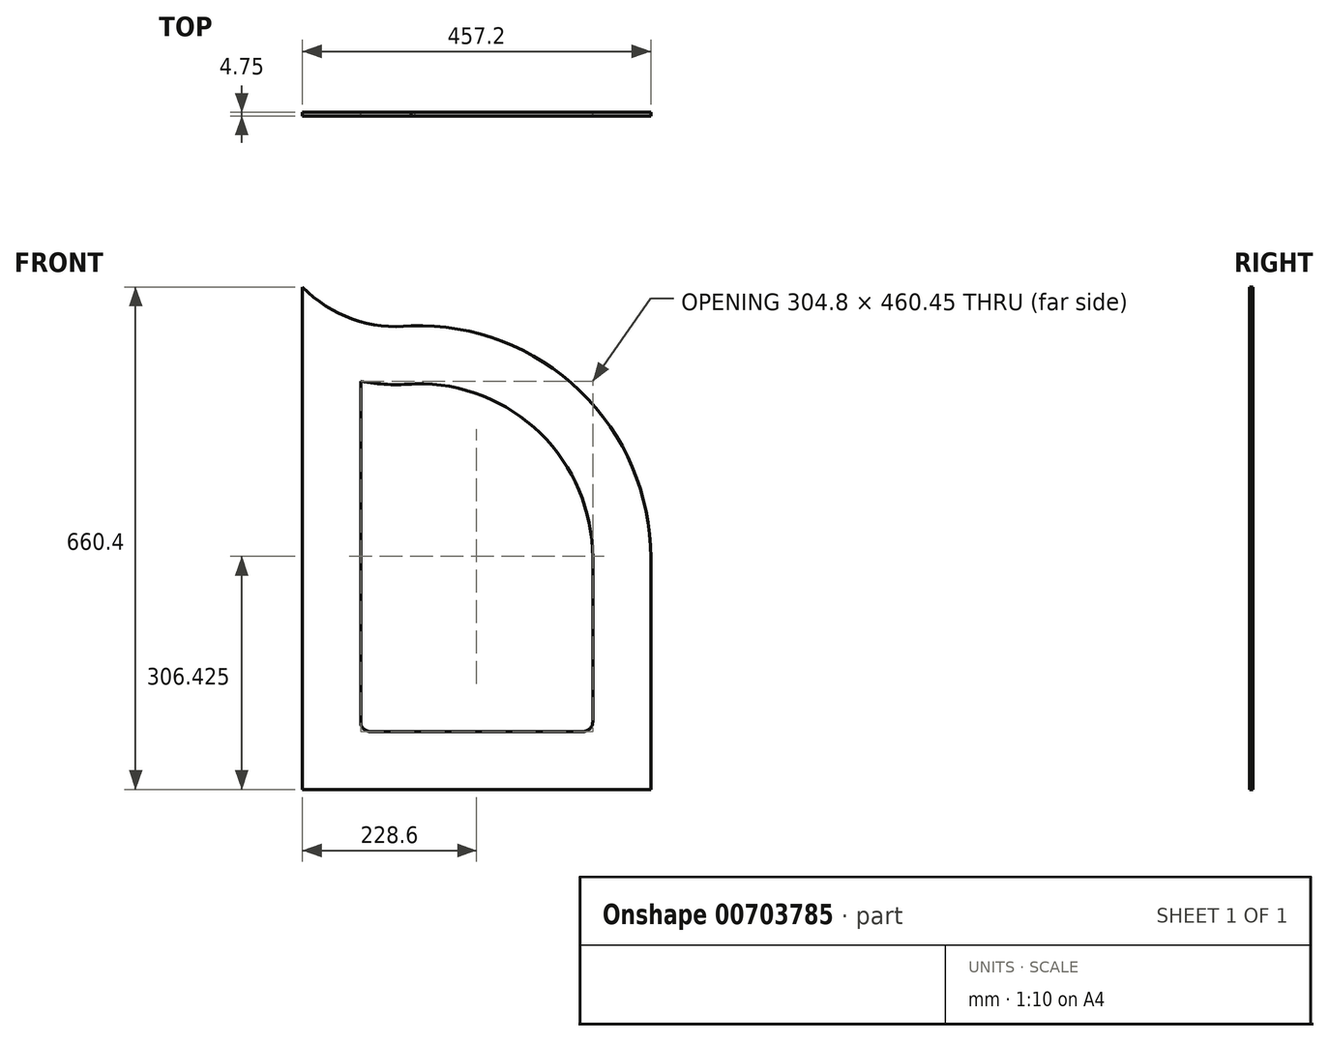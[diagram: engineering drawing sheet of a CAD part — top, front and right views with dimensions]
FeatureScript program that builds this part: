
annotation { "Feature Type Name" : "Feature", "Feature Type Description" : "" }
export const myFeature = defineFeature(function(context is Context, id is Id, definition is map)
    precondition{}
    {
        {
            var Q0;
            Q0=qCreatedBy(makeId("Front.planeOp"),FACE);
            var sketch = newSketch(context, id + "F0", { "sketchPlane" : qUnion([Q0])});
            skArc(sketch, "E0", {"start": v(304.8, 0) * mm, "mid": v(211.94, 219.05) * mm, "end": v(-10.05, 304.63) * mm});
            skLineSegment(sketch, "E1", {"start": v(304.8, 0) * mm, "end": v(304.8, -304.8) * mm});
            skLineSegment(sketch, "E2", {"start": v(304.8, -304.8) * mm, "end": v(0, -304.8) * mm});
            skLineSegment(sketch, "E3", {"start": v(0, -304.8) * mm, "end": v(-152.4, -304.8) * mm});
            skLineSegment(sketch, "E4", {"start": v(-152.4, -304.8) * mm, "end": v(-152.4, 355.6) * mm});
            skArc(sketch, "E5", {"start": v(-152.4, 355.6) * mm, "mid": v(-87.13, 313.61) * mm, "end": v(-10.05, 304.63) * mm});
            skArc(sketch, "E6.0", {"start": v(228.6, 0) * mm, "mid": v(159.86, 163.4) * mm, "end": v(-5.02, 228.54) * mm});
            skLineSegment(sketch, "E6.1", {"start": v(215.9, -228.6) * mm, "end": v(0, -228.6) * mm});
            skLineSegment(sketch, "E6.2", {"start": v(0, -228.6) * mm, "end": v(-63.5, -228.6) * mm});
            skLineSegment(sketch, "E6.3", {"start": v(228.6, 0) * mm, "end": v(228.6, -215.9) * mm});
            skLineSegment(sketch, "E6.4", {"start": v(-76.2, -215.9) * mm, "end": v(-76.2, 231.85) * mm});
            skArc(sketch, "E6.5", {"start": v(-76.2, 231.85) * mm, "mid": v(-40.73, 227.63) * mm, "end": v(-5.02, 228.54) * mm});
            skPoint(sketch, "E7.centerSnap0", {"position": v(-165.7, -341.01) * mm});
            skPoint(sketch, "E8.centerSnap0", {"position": v(304.8, -345.31) * mm});
            skPoint(sketch, "E9.visualSharp", {"position": v(-179.02, -377.23) * mm});
            skPoint(sketch, "E10.visualSharp", {"position": v(-76.2, -228.6) * mm});
            skArc(sketch, "E10.filletArc", {"start": v(-76.2, -215.9) * mm, "mid": v(-72.48, -224.88) * mm, "end": v(-63.5, -228.6) * mm});
            skPoint(sketch, "E11.visualSharp", {"position": v(304.8, -385.82) * mm});
            skPoint(sketch, "E12.visualSharp", {"position": v(228.6, -228.6) * mm});
            skArc(sketch, "E12.filletArc", {"start": v(215.9, -228.6) * mm, "mid": v(224.88, -224.88) * mm, "end": v(228.6, -215.9) * mm});
            skPoint(sketch, "E7.center.orphan", {"position": v(-44.45, -341.01) * mm});
            skPoint(sketch, "E13.center.orphan", {"position": v(-76.2, -341.01) * mm});
            skPoint(sketch, "E13.end.orphan", {"position": v(-76.2, -351.66) * mm});
            skPoint(sketch, "E13.start.orphan", {"position": v(-76.2, -338.96) * mm});
            skPoint(sketch, "E8.center.orphan", {"position": v(228.6, -345.31) * mm});
            skPoint(sketch, "E14.center.orphan", {"position": v(196.85, -345.31) * mm});
            skPoint(sketch, "E14.end.orphan", {"position": v(196.85, -351.66) * mm});
            skPoint(sketch, "E14.start.orphan", {"position": v(196.85, -338.96) * mm});
            skSolve(sketch);
        }
        {
            var Q0;
            Q0=makeQuery(id+"F0.imprint","IMPRINT",FACE,{"disambiguationData":[TD([[makeQuery(id+"F0.imprint","IMPRINT",EDGE,{"derivedFrom":sQuery(id+"F0.wireOp",EDGE,"E0")}),1.0]])]});
            var Q1;
            Q1=makeQuery(id+"F0.imprint","IMPRINT",FACE,{"disambiguationData":[TD([[makeQuery(id+"F0.imprint","IMPRINT",EDGE,{"derivedFrom":sQuery(id+"F0.wireOp",EDGE,"E2")}),1.0]])]});
            extrude(context, id + "F1", {"entities" : qUnion([Q0, Q1]), "depth" : 4.75 * mm, "offsetDistance" : 25.4 * mm});
        }
    });
